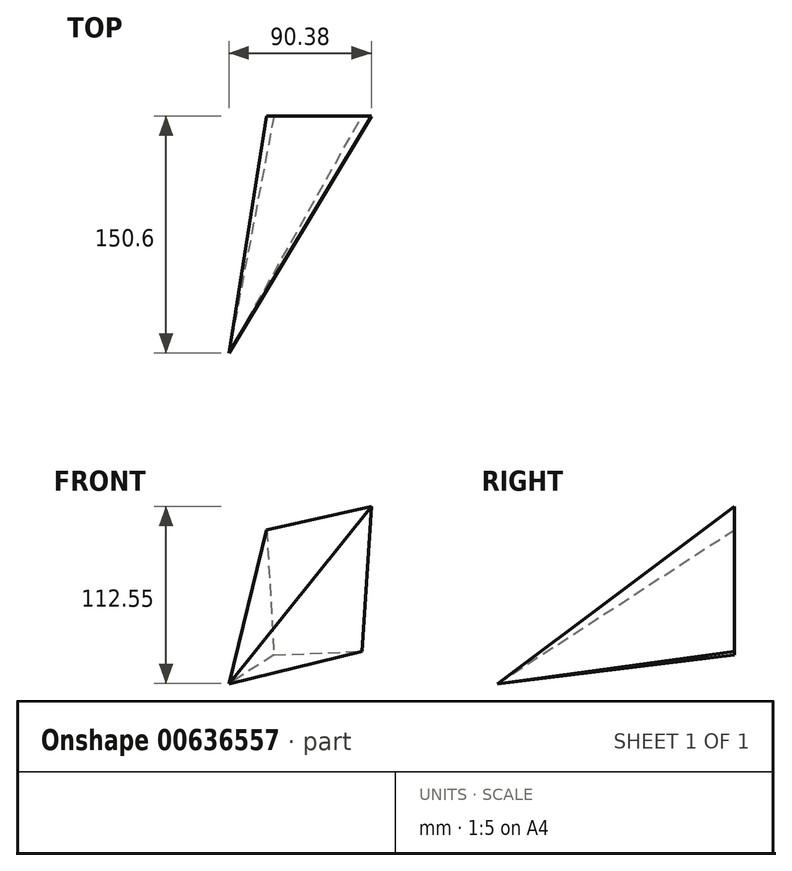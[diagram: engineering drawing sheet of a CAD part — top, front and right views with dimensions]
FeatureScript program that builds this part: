
annotation { "Feature Type Name" : "Feature", "Feature Type Description" : "" }
export const myFeature = defineFeature(function(context is Context, id is Id, definition is map)
    precondition{}
    {
        {
            var Q0;
            Q0=qCreatedBy(makeId("Front.planeOp"),FACE);
            var sketch = newSketch(context, id + "F0", { "sketchPlane" : qUnion([Q0])});
            skLineSegment(sketch, "E0.bottom", {"start": v(0, 140) * mm, "end": v(100, 140) * mm});
            skLineSegment(sketch, "E0.top", {"start": v(0, 0) * mm, "end": v(100, 0) * mm});
            skLineSegment(sketch, "E0.left", {"start": v(0, 140) * mm, "end": v(0, 0) * mm});
            skLineSegment(sketch, "E0.right", {"start": v(100, 140) * mm, "end": v(100, 0) * mm});
            skSolve(sketch);
        }
        {
            var Q0;
            Q0 = qSketchRegion(id + "F0", true);
            extrude(context, id + "F1", {"entities" : qUnion([Q0]), "depth" : 300 * mm, "offsetDistance" : 25 * mm});
        }
        {
            var Q0;
            Q0=makeQuery(id+"F1.opExtrude","SWEPT_FACE",FACE,{"disambiguationData":[OSD([sQuery(id+"F0.wireOp",EDGE,"E0.bottom")])]});
            var sketch = newSketch(context, id + "F2", { "sketchPlane" : qUnion([Q0])});
            skLineSegment(sketch, "E1", {"start": v(0, 0) * mm, "end": v(50, -300) * mm});
            skLineSegment(sketch, "E2", {"start": v(50, -300) * mm, "end": v(100, 0) * mm});
            skLineSegment(sketch, "E3", {"start": v(0, 0) * mm, "end": v(-43.49, -321.47) * mm});
            skLineSegment(sketch, "E4", {"start": v(-43.49, -321.47) * mm, "end": v(163.46, -380.99) * mm});
            skLineSegment(sketch, "E5", {"start": v(163.46, -380.99) * mm, "end": v(100, 0) * mm});
            skSolve(sketch);
        }
        {
            var Q0;
            Q0=makeQuery(id+"F1.opExtrude","SWEPT_FACE",FACE,{"disambiguationData":[OSD([sQuery(id+"F0.wireOp",EDGE,"E0.right")])]});
            var sketch = newSketch(context, id + "F3", { "sketchPlane" : qUnion([Q0])});
            skLineSegment(sketch, "E6", {"start": v(0, 140) * mm, "end": v(-300, 70) * mm});
            skLineSegment(sketch, "E7", {"start": v(-300, 70) * mm, "end": v(0, 0) * mm});
            skLineSegment(sketch, "E8", {"start": v(0, 0) * mm, "end": v(-333.83, -23.5) * mm});
            skLineSegment(sketch, "E9", {"start": v(-333.83, -23.5) * mm, "end": v(-333.83, 174.13) * mm});
            skLineSegment(sketch, "E10", {"start": v(-333.83, 174.13) * mm, "end": v(0, 140) * mm});
            skSolve(sketch);
        }
        {
            var Q0;
            Q0 = qSketchRegion(id + "F2", true);
            extrude(context, id + "F4", {"entities" : qUnion([Q0]), "operationType" : NewBodyOperationType.REMOVE, "endBound" : BoundingType.THROUGH_ALL, "oppositeDirection" : true, "depth" : 25 * mm, "offsetDistance" : 25 * mm});
        }
        {
            var Q0;
            Q0 = qSketchRegion(id + "F3", true);
            extrude(context, id + "F5", {"entities" : qUnion([Q0]), "operationType" : NewBodyOperationType.REMOVE, "endBound" : BoundingType.THROUGH_ALL, "oppositeDirection" : true, "depth" : 25 * mm, "offsetDistance" : 25 * mm});
        }
        {
            var Q0;
            Q0=makeQuery(id+"F1.opExtrude","SWEPT_BODY",BODY,{"disambiguationData":[OSD([sQuery(id+"F0.wireOp",EDGE,"E0.bottom"),sQuery(id+"F0.wireOp",EDGE,"E0.top"),sQuery(id+"F0.wireOp",EDGE,"E0.left"),sQuery(id+"F0.wireOp",EDGE,"E0.right")])]});
            var Q1;
            {var subQ0=sQuery(id+"F0.wireOp",EDGE,"E0.right");Q1=makeQuery(id+"F4.boolean.opBoolean","MERGE",EDGE,{"derivedFrom":[makeQuery(id+"F1.opExtrude","CAP_EDGE",EDGE,{"disambiguationData":[OSD([subQ0])],"isStart":true}),makeQuery(id+"F4.opExtrude","SWEPT_EDGE",EDGE,{"disambiguationData":[OSD([sQuery(id+"F0.wireOp",EDGE,"E0.bottom"),subQ0,sQuery(id+"F2.wireOp",EDGE,"E2"),sQuery(id+"F2.wireOp",EDGE,"E5")])]})]});}
            transform(context, id + "F6", {"entities" : qUnion([Q0]), "transformType" : TransformType.ROTATION, "transformAxis" : qUnion([Q1]), "angle" : 20 * degree, "makeCopy" : false});
        }
        {
            var Q0;
            Q0=makeQuery(id+"F1.opExtrude","SWEPT_BODY",BODY,{"disambiguationData":[OSD([sQuery(id+"F0.wireOp",EDGE,"E0.bottom"),sQuery(id+"F0.wireOp",EDGE,"E0.top"),sQuery(id+"F0.wireOp",EDGE,"E0.left"),sQuery(id+"F0.wireOp",EDGE,"E0.right")])]});
            var Q1;
            {var subQ0=sQuery(id+"F0.wireOp",EDGE,"E0.bottom");Q1=makeQuery(id+"F5.boolean.opBoolean","MERGE",EDGE,{"derivedFrom":[makeQuery(id+"F1.opExtrude","CAP_EDGE",EDGE,{"disambiguationData":[OSD([subQ0])],"isStart":true}),makeQuery(id+"F5.opExtrude","SWEPT_EDGE",EDGE,{"disambiguationData":[OSD([subQ0,sQuery(id+"F0.wireOp",EDGE,"E0.right"),sQuery(id+"F3.wireOp",EDGE,"E6"),sQuery(id+"F3.wireOp",EDGE,"E10")])]})]});}
            transform(context, id + "F7", {"entities" : qUnion([Q0]), "transformType" : TransformType.ROTATION, "transformAxis" : qUnion([Q1]), "angle" : 20 * degree, "makeCopy" : false});
        }
        {
            var Q0;
            Q0=qCreatedBy(makeId("Top.planeOp"),FACE);
            var sketch = newSketch(context, id + "F8", { "sketchPlane" : qUnion([Q0])});
            skLineSegment(sketch, "E11", {"start": v(-35.28, -224.7) * mm, "end": v(-35.28, 0) * mm, "construction": true});
            skLineSegment(sketch, "E12.bottom", {"start": v(-78.52, -74.7) * mm, "end": v(133.72, -74.7) * mm});
            skLineSegment(sketch, "E12.top", {"start": v(-78.52, 124.17) * mm, "end": v(133.72, 124.17) * mm});
            skLineSegment(sketch, "E12.left", {"start": v(-78.52, -74.7) * mm, "end": v(-78.52, 124.17) * mm});
            skLineSegment(sketch, "E12.right", {"start": v(133.72, -74.7) * mm, "end": v(133.72, 124.17) * mm});
            skSolve(sketch);
        }
        {
            var Q0;
            Q0 = qSketchRegion(id + "F8", true);
            extrude(context, id + "F9", {"entities" : qUnion([Q0]), "operationType" : NewBodyOperationType.REMOVE, "endBound" : BoundingType.SYMMETRIC, "depth" : 284 * mm, "offsetDistance" : 25 * mm});
        }
    });
